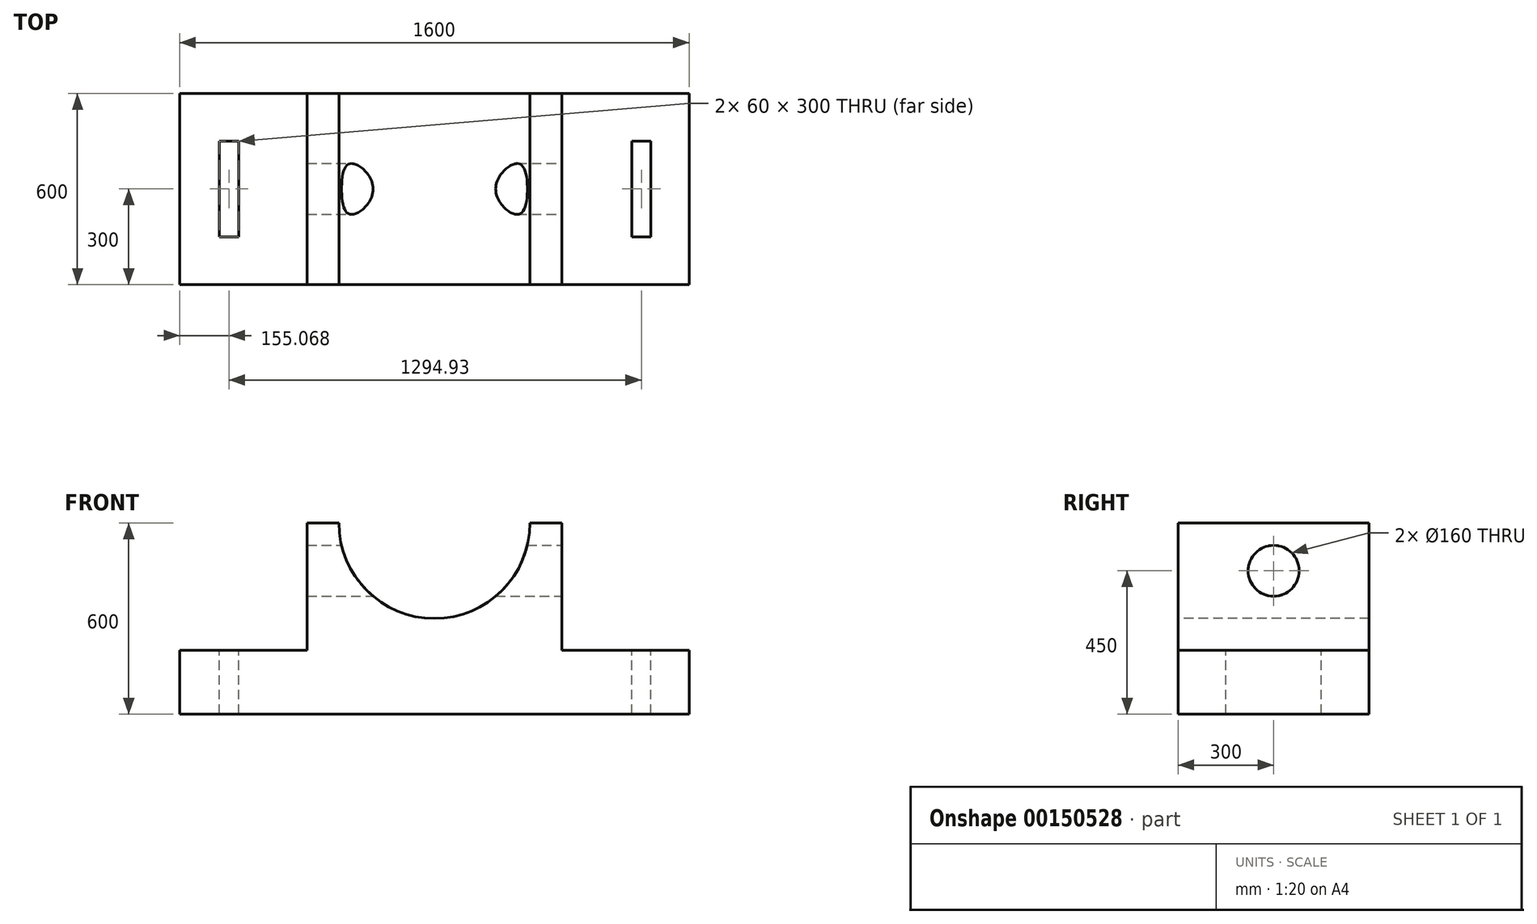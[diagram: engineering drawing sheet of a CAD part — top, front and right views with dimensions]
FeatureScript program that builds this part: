
annotation { "Feature Type Name" : "Feature", "Feature Type Description" : "" }
export const myFeature = defineFeature(function(context is Context, id is Id, definition is map)
    precondition{}
    {
        {
            var Q0;
            Q0=qCreatedBy(makeId("Top.planeOp"),FACE);
            var sketch = newSketch(context, id + "F0", { "sketchPlane" : qUnion([Q0])});
            skLineSegment(sketch, "E0.bottom", {"start": v(-800, -300) * mm, "end": v(800, -300) * mm});
            skLineSegment(sketch, "E0.top", {"start": v(-800, 300) * mm, "end": v(800, 300) * mm});
            skLineSegment(sketch, "E0.left", {"start": v(-800, -300) * mm, "end": v(-800, 300) * mm});
            skLineSegment(sketch, "E0.right", {"start": v(800, -300) * mm, "end": v(800, 300) * mm});
            skPoint(sketch, "E0.middle", {"position": v(0, 0) * mm});
            skSolve(sketch);
        }
        {
            var Q0;
            Q0=makeQuery(id+"F0.imprint","IMPRINT",FACE,{"disambiguationData":[TD([[makeQuery(id+"F0.imprint","IMPRINT",EDGE,{"derivedFrom":sQuery(id+"F0.wireOp",EDGE,"E0.bottom")}),1.0]])]});
            extrude(context, id + "F1", {"entities" : qUnion([Q0]), "depth" : 600 * mm});
        }
        {
            var Q0;
            Q0=makeQuery(id+"F1.opExtrude","SWEPT_FACE",FACE,{"disambiguationData":[OSD([sQuery(id+"F0.wireOp",EDGE,"E0.bottom")])]});
            var sketch = newSketch(context, id + "F2", { "sketchPlane" : qUnion([Q0])});
            skCircle(sketch, "E1", {"center": v(0, 600) * mm, "radius": 300 * mm});
            skSolve(sketch);
        }
        {
            var Q0;
            {var subQ0=sQuery(id+"F2.wireOp",EDGE,"E1");var subQ1=makeQuery(id+"F1.opExtrude","CAP_EDGE",EDGE,{"disambiguationData":[OSD([sQuery(id+"F0.wireOp",EDGE,"E0.bottom")])],"isStart":false});var subQ2=makeQuery(id+"F2.imprint","INTERSECT",VERTEX,{"disambiguationData":[OD(0.0)],"derivedFrom":[subQ1,subQ0]});Q0=makeQuery(id+"F2.imprint","IMPRINT",FACE,{"disambiguationData":[TD([[makeQuery(id+"F2.imprint","IMPRINT",EDGE,{"disambiguationData":[TD([[subQ2,-1.0]])],"derivedFrom":subQ0}),1.0]])]});}
            extrude(context, id + "F3", {"entities" : qUnion([Q0]), "operationType" : NewBodyOperationType.REMOVE, "endBound" : BoundingType.THROUGH_ALL, "oppositeDirection" : true, "depth" : 25 * mm});
        }
        {
            var Q0;
            {var subQ0=sQuery(id+"F0.wireOp",EDGE,"E0.bottom");var subQ1=sQuery(id+"F0.wireOp",EDGE,"E0.top");var subQ2=sQuery(id+"F0.wireOp",EDGE,"E0.left");Q0=makeQuery(id+"F3.boolean.opBoolean","SPLIT",FACE,{"disambiguationData":[TD([makeQuery(id+"F1.opExtrude","SWEPT_FACE",FACE,{"disambiguationData":[OSD([subQ2])]})])],"derivedFrom":makeQuery(id+"F1.opExtrude","CAP_FACE",FACE,{"disambiguationData":[OSD([subQ0,subQ1,subQ2,sQuery(id+"F0.wireOp",EDGE,"E0.right")])],"isStart":false})});}
            var sketch = newSketch(context, id + "F4", { "sketchPlane" : qUnion([Q0])});
            skSolve(sketch);
        }
        {
            var Q0;
            Q0=makeQuery(id+"F1.opExtrude","SWEPT_FACE",FACE,{"disambiguationData":[OSD([sQuery(id+"F0.wireOp",EDGE,"E0.bottom")])]});
            var sketch = newSketch(context, id + "F5", { "sketchPlane" : qUnion([Q0])});
            skLineSegment(sketch, "E2.bottom", {"start": v(800, 600) * mm, "end": v(400, 600) * mm});
            skLineSegment(sketch, "E2.top", {"start": v(800, 200) * mm, "end": v(400, 200) * mm});
            skLineSegment(sketch, "E2.left", {"start": v(800, 600) * mm, "end": v(800, 200) * mm});
            skLineSegment(sketch, "E2.right", {"start": v(400, 600) * mm, "end": v(400, 200) * mm});
            skPoint(sketch, "E2.middle", {"position": v(600, 400) * mm});
            skSolve(sketch);
        }
        {
            var Q0;
            Q0=makeQuery(id+"F5.imprint","IMPRINT",FACE,{"disambiguationData":[TD([[makeQuery(id+"F5.imprint","IMPRINT",EDGE,{"derivedFrom":sQuery(id+"F5.wireOp",EDGE,"E2.bottom")}),-1.0]])]});
            extrude(context, id + "F6", {"entities" : qUnion([Q0]), "operationType" : NewBodyOperationType.REMOVE, "endBound" : BoundingType.THROUGH_ALL, "oppositeDirection" : true, "depth" : 25 * mm});
        }
        {
            var Q0;
            Q0=makeQuery(id+"F1.opExtrude","SWEPT_FACE",FACE,{"disambiguationData":[OSD([sQuery(id+"F0.wireOp",EDGE,"E0.bottom")])]});
            var sketch = newSketch(context, id + "F7", { "sketchPlane" : qUnion([Q0])});
            skLineSegment(sketch, "E3.bottom", {"start": v(-400, 200) * mm, "end": v(-1200, 200) * mm});
            skLineSegment(sketch, "E3.top", {"start": v(-400, 1000) * mm, "end": v(-1200, 1000) * mm});
            skLineSegment(sketch, "E3.left", {"start": v(-400, 200) * mm, "end": v(-400, 1000) * mm});
            skLineSegment(sketch, "E3.right", {"start": v(-1200, 200) * mm, "end": v(-1200, 1000) * mm});
            skPoint(sketch, "E3.middle", {"position": v(-800, 600) * mm});
            skSolve(sketch);
        }
        {
            var Q0;
            {var subQ0=sQuery(id+"F7.wireOp",EDGE,"E3.left");var subQ1=sQuery(id+"F7.wireOp",EDGE,"E3.bottom");var subQ2=makeQuery(id+"F7.imprint","INTERSECT",VERTEX,{"derivedFrom":[subQ1,subQ0]});Q0=makeQuery(id+"F7.imprint","IMPRINT",FACE,{"disambiguationData":[TD([[makeQuery(id+"F7.imprint","IMPRINT",EDGE,{"disambiguationData":[TD([[subQ2,-1.0]])],"derivedFrom":subQ1}),-1.0]])]});}
            extrude(context, id + "F8", {"entities" : qUnion([Q0]), "operationType" : NewBodyOperationType.REMOVE, "endBound" : BoundingType.THROUGH_ALL, "oppositeDirection" : true, "depth" : 25 * mm});
        }
        {
            var Q0;
            Q0=makeQuery(id+"F6.boolean.opBoolean","COPY",FACE,{"derivedFrom":makeQuery(id+"F6.opExtrude","SWEPT_FACE",FACE,{"disambiguationData":[OSD([sQuery(id+"F5.wireOp",EDGE,"E2.right")])]})});
            var sketch = newSketch(context, id + "F9", { "sketchPlane" : qUnion([Q0])});
            skLineSegment(sketch, "E4", {"start": v(0, 0) * mm, "end": v(0, 450) * mm});
            skPoint(sketch, "E4.endSnap0", {"position": v(0, 200) * mm});
            skCircle(sketch, "E5", {"center": v(0, 450) * mm, "radius": 80 * mm});
            skSolve(sketch);
        }
        {
            var Q0;
            Q0=makeQuery(id+"F9.imprint","IMPRINT",FACE,{"disambiguationData":[TD([[makeQuery(id+"F9.imprint","IMPRINT",EDGE,{"derivedFrom":sQuery(id+"F9.wireOp",EDGE,"E5")}),1.0]])]});
            extrude(context, id + "F10", {"entities" : qUnion([Q0]), "operationType" : NewBodyOperationType.REMOVE, "oppositeDirection" : true, "depth" : 1400 * mm});
        }
        {
            var Q0;
            Q0=makeQuery(id+"F6.boolean.opBoolean","COPY",FACE,{"derivedFrom":makeQuery(id+"F6.opExtrude","SWEPT_FACE",FACE,{"disambiguationData":[OSD([sQuery(id+"F5.wireOp",EDGE,"E2.top")])]})});
            var sketch = newSketch(context, id + "F11", { "sketchPlane" : qUnion([Q0])});
            skLineSegment(sketch, "E6", {"start": v(800, 0) * mm, "end": v(650, 0) * mm});
            skPoint(sketch, "E6.endSnap0", {"position": v(800, 0) * mm});
            skLineSegment(sketch, "E7.bottom", {"start": v(620, -150) * mm, "end": v(680, -150) * mm});
            skLineSegment(sketch, "E7.top", {"start": v(620, 150) * mm, "end": v(680, 150) * mm});
            skLineSegment(sketch, "E7.left", {"start": v(620, -150) * mm, "end": v(620, 150) * mm});
            skLineSegment(sketch, "E7.right", {"start": v(680, -150) * mm, "end": v(680, 150) * mm});
            skPoint(sketch, "E7.middle", {"position": v(650, 0) * mm});
            skSolve(sketch);
        }
        {
            var Q0;
            {var subQ1=sQuery(id+"F11.wireOp",EDGE,"E7.bottom");Q0=makeQuery(id+"F11.imprint","IMPRINT",FACE,{"disambiguationData":[TD([[makeQuery(id+"F11.imprint","IMPRINT",EDGE,{"derivedFrom":subQ1}),1.0]])]});}
            extrude(context, id + "F12", {"entities" : qUnion([Q0]), "operationType" : NewBodyOperationType.REMOVE, "endBound" : BoundingType.THROUGH_ALL, "oppositeDirection" : true, "depth" : 25 * mm});
        }
        {
            var Q0;
            {var subQ0=sQuery(id+"F0.wireOp",EDGE,"E0.left");Q0=makeQuery(id+"F4.imprint","IMPRINT",FACE,{"disambiguationData":[TD([[makeQuery(id+"F4.imprint","IMPRINT",EDGE,{"derivedFrom":makeQuery(id+"F1.opExtrude","CAP_EDGE",EDGE,{"disambiguationData":[OSD([subQ0])],"isStart":false})}),-1.0]])]});}
            var sketch = newSketch(context, id + "F13", { "sketchPlane" : qUnion([Q0])});
            skLineSegment(sketch, "E8", {"start": v(-794.93, 0) * mm, "end": v(-644.93, 0) * mm});
            skLineSegment(sketch, "E9.bottom", {"start": v(-674.93, -150) * mm, "end": v(-614.93, -150) * mm});
            skLineSegment(sketch, "E9.top", {"start": v(-674.93, 150) * mm, "end": v(-614.93, 150) * mm});
            skLineSegment(sketch, "E9.left", {"start": v(-674.93, -150) * mm, "end": v(-674.93, 150) * mm});
            skLineSegment(sketch, "E9.right", {"start": v(-614.93, -150) * mm, "end": v(-614.93, 150) * mm});
            skPoint(sketch, "E9.middle", {"position": v(-644.93, 0) * mm});
            skSolve(sketch);
        }
        {
            var Q0;
            {var subQ3=sQuery(id+"F13.wireOp",EDGE,"E9.bottom");Q0=makeQuery(id+"F13.imprint","IMPRINT",FACE,{"disambiguationData":[TD([[makeQuery(id+"F13.imprint","IMPRINT",EDGE,{"derivedFrom":subQ3}),1.0]])]});}
            extrude(context, id + "F14", {"entities" : qUnion([Q0]), "operationType" : NewBodyOperationType.REMOVE, "endBound" : BoundingType.THROUGH_ALL, "oppositeDirection" : true, "depth" : 25 * mm});
        }
    });
